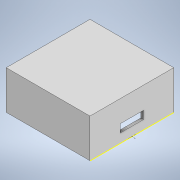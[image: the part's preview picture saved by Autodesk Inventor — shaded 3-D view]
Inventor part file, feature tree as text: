
AUTODESK INVENTOR PART (.ipt)
format: ipt  version: 2022 (Build 260153000, 153)  size: 131,072 bytes
history: native  units: in
note: dims shown in document units (in); Inventor stores cm internally (conversion verified against a paired STEP export)
features: sketch x5, extrude x4
ambient origin geometry x8: Origin, YZ Plane, XZ Plane, XY Plane, X Axis, Y Axis, Z Axis, Center Point
bodies: Solid1 (feature_tree)
feature tree (9):
  extrude  "Extrusion1"  Depth=0.2165in
  extrude  "Extrusion2"  Depth=0.2559in
  sketch  "Sketch5"  dims[d8=0.0787in d9=0.0in d10=0.2559in]
  extrude  "Extrusion3"  Depth=0.2559in
  extrude  "Extrusion4"  Depth=0.0394in
  sketch  "Sketch2"  dims[d2=0.2165in d3=0.2165in]
  sketch  "Sketch4"  dims[d6=0.2559in d7=0.2559in]
  sketch  "Sketch6"  dims[d11=0.0394in d12=0.0in d13=0.0945in]
  sketch  "Sketch7"  dims[d14=0.0472in d15=0.0394in d16=0.0197in d17=-0.2061in d18=0.0945in d19=0.0472in d20=0.0394in d21=0.0197in d22=-0.2061in]
